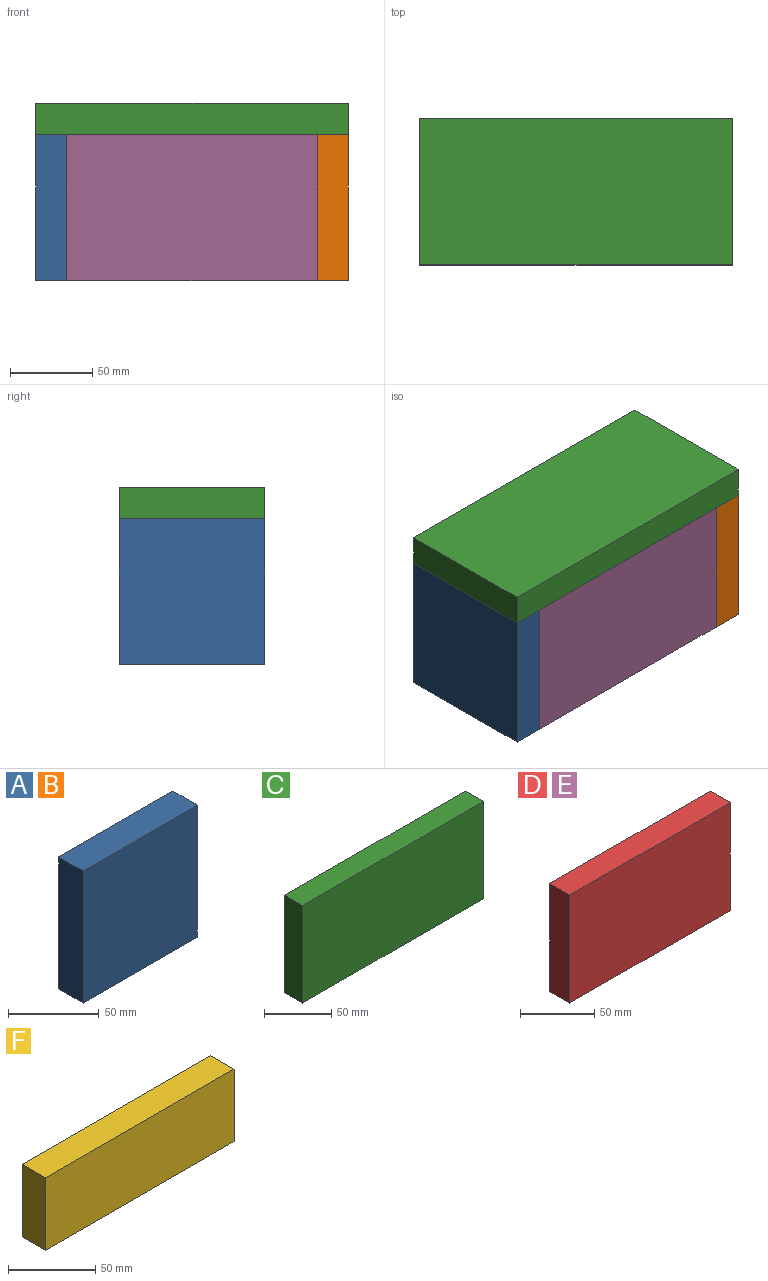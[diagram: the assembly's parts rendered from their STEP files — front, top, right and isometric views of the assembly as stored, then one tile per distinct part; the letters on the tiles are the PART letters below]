
ASSEMBLY  parts=6 mates=13
PART A: 6 faces, bbox 88.9x19.1x88.9 mm
  f0: plane 88.9x19.05mm, normal (0,0,-1), area 1693.5mm2, adj f1,f3,f4,f5
  f1: plane 88.9x19.05mm, normal (1,0,0), area 1693.5mm2, adj f0,f2,f4,f5
  f2: plane 88.9x19.05mm, normal (0,0,1), area 1693.5mm2, adj f1,f3,f4,f5
  f3: plane 88.9x19.05mm, normal (-1,0,0), area 1693.5mm2, adj f0,f2,f4,f5
  f4: plane 88.9x88.9mm, normal (0,-1,0), area 7903.2mm2, adj f0,f1,f2,f3
  f5: plane 88.9x88.9mm, normal (0,1,0), area 7903.2mm2, adj f0,f1,f2,f3
PART B: same geometry as A
PART C: 6 faces, bbox 190.5x19.1x88.9 mm
  f0: plane 88.9x19.05mm, normal (1,0,0), area 1693.5mm2, adj f1,f3,f4,f5
  f1: plane 190.5x19.05mm, normal (0,0,1), area 3629mm2, adj f0,f2,f4,f5
  f2: plane 88.9x19.05mm, normal (-1,0,0), area 1693.5mm2, adj f1,f3,f4,f5
  f3: plane 190.5x19.05mm, normal (0,0,-1), area 3629mm2, adj f0,f2,f4,f5
  f4: plane 190.5x88.9mm, normal (0,-1,0), area 16935.5mm2, adj f0,f1,f2,f3
  f5: plane 190.5x88.9mm, normal (0,1,0), area 16935.5mm2, adj f0,f1,f2,f3
PART D: 6 faces, bbox 152.4x19.1x88.9 mm
  f0: plane 88.9x19.05mm, normal (-1,0,0), area 1693.5mm2, adj f1,f3,f4,f5
  f1: plane 152.4x19.05mm, normal (0,0,-1), area 2903.2mm2, adj f0,f2,f4,f5
  f2: plane 88.9x19.05mm, normal (1,0,0), area 1693.5mm2, adj f1,f3,f4,f5
  f3: plane 152.4x19.05mm, normal (0,0,1), area 2903.2mm2, adj f0,f2,f4,f5
  f4: plane 152.4x88.9mm, normal (0,-1,0), area 13548.4mm2, adj f0,f1,f2,f3
  f5: plane 152.4x88.9mm, normal (0,1,0), area 13548.4mm2, adj f0,f1,f2,f3
PART E: same geometry as D
PART F: 6 faces, bbox 152.4x19.1x50.8 mm
  f0: plane 152.4x19.05mm, normal (0,0,1), area 2903.2mm2, adj f1,f3,f4,f5
  f1: plane 50.8x19.05mm, normal (-1,0,0), area 967.7mm2, adj f0,f2,f4,f5
  f2: plane 152.4x19.05mm, normal (0,0,-1), area 2903.2mm2, adj f1,f3,f4,f5
  f3: plane 50.8x19.05mm, normal (1,0,0), area 967.7mm2, adj f0,f2,f4,f5
  f4: plane 152.4x50.8mm, normal (0,-1,0), area 7741.9mm2, adj f0,f1,f2,f3
  f5: plane 152.4x50.8mm, normal (0,1,0), area 7741.9mm2, adj f0,f1,f2,f3
PLACE A rot(axis=(0.71,0.71,0),180deg) t=(0,25.92,88.9)mm
PLACE B rot(axis=(0.71,-0.71,0),180deg) t=(152.4,-114.82,88.9)mm
PLACE C rot(axis=(1,0,0),90deg) t=(180.65,-108.78,107.95)mm
PLACE D at identity fixed
PLACE E t=(0,-69.85,0)mm
PLACE F rot(axis=(-1,0,0),90deg) t=(0,1.33,0)mm
MATE planar D.f1 <-> F.f5  axis (0,0,-1) through (76.2,-9.53,0)mm
MATE planar E.f5 <-> F.f2  axis (0,1,0) through (76.2,-69.85,44.45)mm
MATE planar A.f5 <-> F.f1  axis (1,0,0) through (0,-44.45,44.45)mm
MATE planar B.f5 <-> F.f3  axis (-1,0,0) through (152.4,-44.45,44.45)mm
MATE planar D.f0 <-> F.f1  axis (-1,0,0) through (0,-9.53,44.45)mm
MATE planar B.f2 <-> F.f5  axis (0,0,-1) through (161.93,-44.45,0)mm
MATE planar D.f3 <-> C.f4  axis (0,0,1) through (76.2,-9.53,88.9)mm
MATE planar F.f0 <-> D.f4  axis (0,1,0) through (76.2,-19.05,9.53)mm
MATE planar C.f1 <-> E.f4  axis (0,-1,0) through (-19.05,-88.9,88.9)mm
MATE planar F.f1 <-> E.f0  axis (-1,0,0) through (0,-44.45,9.53)mm
MATE planar E.f1 <-> F.f5  axis (0,0,-1) through (76.2,-79.38,0)mm
MATE planar A.f2 <-> F.f5  axis (0,0,-1) through (-9.53,-44.45,0)mm
MATE planar C.f2 <-> A.f4  axis (-1,0,0) through (-19.05,-44.45,98.42)mm
